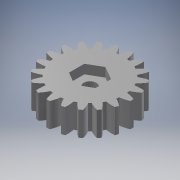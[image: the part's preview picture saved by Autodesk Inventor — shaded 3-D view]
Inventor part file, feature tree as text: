
AUTODESK INVENTOR PART (.ipt)
format: ipt  version: 2017 (Build 210142000, 142)  size: 235,520 bytes
history: native  units: mm (DEFAULTED — no unit token found)
features: sketch x4, extrude x3, plane x3, other x3
ambient origin geometry x8: Origin, YZ Plane, XZ Plane, XY Plane, X Axis, Y Axis, Z Axis, Center Point
bodies: Solid1 (feature_tree)
feature tree (13):
  extrude  "Extrusion1"  Depth=8.0mm TaperAngle=0.0deg
  plane  "Work Plane2"
  plane  "Work Plane8"
  plane  "Work Plane9"
  other  "Spur Gear"
  extrude  "Extrusion2"  Depth=10.0mm TaperAngle=0.0deg
  extrude  "Extrusion3"  Depth=1.570796mm TaperAngle=0.0deg
  sketch  "Sketch1"  dims[d0=27.5mm d1=8.0mm d2=0.0mm]
  sketch  "Sketch2"  dims[d3=25.0mm d4=10.0mm d5=0.0mm]
  other  "Srf1"
  sketch  "Sketch3"  dims[d16=21.25mm d17=0.0mm d34=1.570796mm]
  sketch  "Sketch4"  dims[d39=0.0mm d41=0.0mm d43=21.25mm d46=21.25mm d47=0.0mm d48=0.0mm d49=4.1656mm d50=10.0mm d51=0.0mm d52=10.0838mm d53=3.0mm d54=0.0mm]
  other  "Pitch Diameter"
